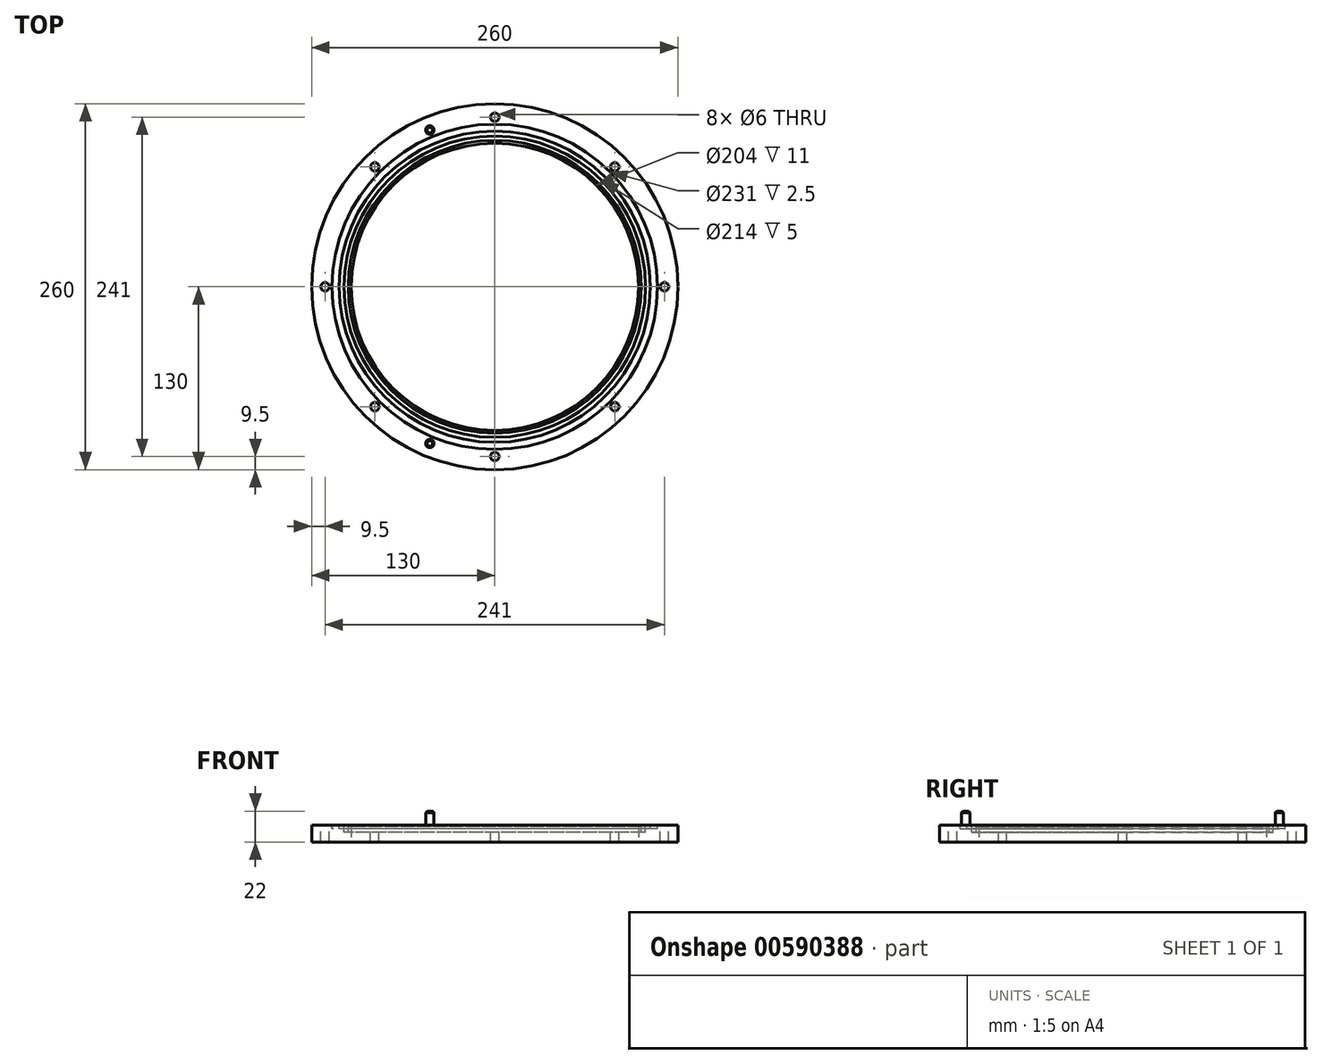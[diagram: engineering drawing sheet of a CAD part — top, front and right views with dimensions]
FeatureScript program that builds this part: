
annotation { "Feature Type Name" : "Feature", "Feature Type Description" : "" }
export const myFeature = defineFeature(function(context is Context, id is Id, definition is map)
    precondition{}
    {
        {
            var Q0;
            Q0=qCreatedBy(makeId("Top.planeOp"),FACE);
            var sketch = newSketch(context, id + "F0", { "sketchPlane" : qUnion([Q0])});
            skCircle(sketch, "E0", {"center": v(0, 0) * mm, "radius": 130 * mm});
            skCircle(sketch, "E1", {"center": v(0, 0) * mm, "radius": 102 * mm});
            skSolve(sketch);
        }
        {
            var Q0;
            Q0=makeQuery(id+"F0.imprint","IMPRINT",FACE,{"disambiguationData":[TD([[makeQuery(id+"F0.imprint","IMPRINT",EDGE,{"derivedFrom":sQuery(id+"F0.wireOp",EDGE,"E0")}),1.0]])]});
            extrude(context, id + "F1", {"entities" : qUnion([Q0]), "depth" : 12 * mm, "offsetDistance" : 25 * mm});
        }
        {
            var Q0;
            Q0=makeQuery(id+"F1.opExtrude","CAP_FACE",FACE,{"disambiguationData":[OSD([sQuery(id+"F0.wireOp",EDGE,"E0"),sQuery(id+"F0.wireOp",EDGE,"E1")])],"isStart":false});
            var sketch = newSketch(context, id + "F2", { "sketchPlane" : qUnion([Q0])});
            skCircle(sketch, "E2", {"center": v(0, 0) * mm, "radius": 115.5 * mm});
            skCircle(sketch, "E3", {"center": v(0, 0) * mm, "radius": 110.5 * mm});
            skSolve(sketch);
        }
        {
            var Q0;
            Q0=makeQuery(id+"F2.imprint","IMPRINT",FACE,{"disambiguationData":[TD([[makeQuery(id+"F2.imprint","IMPRINT",EDGE,{"derivedFrom":sQuery(id+"F2.wireOp",EDGE,"E2")}),1.0]])]});
            extrude(context, id + "F3", {"entities" : qUnion([Q0]), "operationType" : NewBodyOperationType.REMOVE, "oppositeDirection" : true, "depth" : 2.5 * mm, "offsetDistance" : 25 * mm});
        }
        {
            var Q0;
            {var subQ0=sQuery(id+"F0.wireOp",EDGE,"E1");Q0=makeQuery(id+"F3.boolean.opBoolean","SPLIT",FACE,{"disambiguationData":[TD([makeQuery(id+"F1.opExtrude","SWEPT_FACE",FACE,{"disambiguationData":[OSD([subQ0])]})])],"derivedFrom":makeQuery(id+"F1.opExtrude","CAP_FACE",FACE,{"disambiguationData":[OSD([sQuery(id+"F0.wireOp",EDGE,"E0"),subQ0])],"isStart":false})});}
            var sketch = newSketch(context, id + "F4", { "sketchPlane" : qUnion([Q0])});
            skCircle(sketch, "E4", {"center": v(0, 0) * mm, "radius": 107 * mm});
            skCircle(sketch, "E5", {"center": v(0, 0) * mm, "radius": 104 * mm});
            skSolve(sketch);
        }
        {
            var Q0;
            Q0=makeQuery(id+"F4.imprint","IMPRINT",FACE,{"disambiguationData":[TD([[makeQuery(id+"F4.imprint","IMPRINT",EDGE,{"derivedFrom":sQuery(id+"F4.wireOp",EDGE,"E4")}),1.0]])]});
            extrude(context, id + "F5", {"entities" : qUnion([Q0]), "operationType" : NewBodyOperationType.REMOVE, "oppositeDirection" : true, "depth" : 5 * mm, "offsetDistance" : 25 * mm});
        }
        {
            var Q0;
            {var subQ0=sQuery(id+"F0.wireOp",EDGE,"E1");var subQ1=makeQuery(id+"F1.opExtrude","SWEPT_FACE",FACE,{"disambiguationData":[OSD([subQ0])]});Q0=makeQuery(id+"F5.boolean.opBoolean","SPLIT",FACE,{"disambiguationData":[TD([subQ1])],"derivedFrom":makeQuery(id+"F3.boolean.opBoolean","SPLIT",FACE,{"disambiguationData":[TD([subQ1])],"derivedFrom":makeQuery(id+"F1.opExtrude","CAP_FACE",FACE,{"disambiguationData":[OSD([sQuery(id+"F0.wireOp",EDGE,"E0"),subQ0])],"isStart":false})})});}
            var sketch = newSketch(context, id + "F6", { "sketchPlane" : qUnion([Q0])});
            skCircle(sketch, "E6", {"center": v(0, 0) * mm, "radius": 104 * mm});
            skCircle(sketch, "E7", {"center": v(0, 0) * mm, "radius": 102 * mm});
            skSolve(sketch);
        }
        {
            var Q0;
            Q0=makeQuery(id+"F6.imprint","IMPRINT",FACE,{"disambiguationData":[TD([[makeQuery(id+"F6.imprint","IMPRINT",EDGE,{"derivedFrom":sQuery(id+"F6.wireOp",EDGE,"E6")}),1.0]])]});
            extrude(context, id + "F7", {"entities" : qUnion([Q0]), "operationType" : NewBodyOperationType.REMOVE, "oppositeDirection" : true, "depth" : 1 * mm, "offsetDistance" : 25 * mm});
        }
        {
            var Q0;
            {var subQ0=sQuery(id+"F0.wireOp",EDGE,"E0");Q0=makeQuery(id+"F3.boolean.opBoolean","SPLIT",FACE,{"disambiguationData":[TD([makeQuery(id+"F1.opExtrude","SWEPT_FACE",FACE,{"disambiguationData":[OSD([subQ0])]})])],"derivedFrom":makeQuery(id+"F1.opExtrude","CAP_FACE",FACE,{"disambiguationData":[OSD([subQ0,sQuery(id+"F0.wireOp",EDGE,"E1")])],"isStart":false})});}
            var sketch = newSketch(context, id + "F8", { "sketchPlane" : qUnion([Q0])});
            skLineSegment(sketch, "E8", {"start": v(0, 0) * mm, "end": v(0, 130) * mm, "construction": true});
            skLineSegment(sketch, "E9", {"start": v(0, 0) * mm, "end": v(130, 0) * mm, "construction": true});
            skLineSegment(sketch, "E10", {"start": v(0, 0) * mm, "end": v(-130, 0) * mm, "construction": true});
            skLineSegment(sketch, "E11", {"start": v(0, 0) * mm, "end": v(0, -130) * mm, "construction": true});
            skLineSegment(sketch, "E12", {"start": v(0, 0) * mm, "end": v(-91.92, 91.92) * mm, "construction": true});
            skLineSegment(sketch, "E13", {"start": v(0, 0) * mm, "end": v(91.92, 91.92) * mm, "construction": true});
            skLineSegment(sketch, "E14", {"start": v(0, 0) * mm, "end": v(91.92, -91.92) * mm, "construction": true});
            skLineSegment(sketch, "E15", {"start": v(0, 0) * mm, "end": v(-91.92, -91.92) * mm, "construction": true});
            skLineSegment(sketch, "E16", {"start": v(0, 0) * mm, "end": v(-49.75, 120.1) * mm, "construction": true});
            skCircle(sketch, "E17", {"center": v(-120.5, 0) * mm, "radius": 3 * mm});
            skCircle(sketch, "E18", {"center": v(-85.2, 85.2) * mm, "radius": 3 * mm});
            skCircle(sketch, "E19", {"center": v(0, 120.5) * mm, "radius": 3 * mm});
            skCircle(sketch, "E20", {"center": v(0, -120.5) * mm, "radius": 3 * mm});
            skCircle(sketch, "E21", {"center": v(-85.2, -85.2) * mm, "radius": 3 * mm});
            skCircle(sketch, "E22", {"center": v(85.2, -85.2) * mm, "radius": 3 * mm});
            skCircle(sketch, "E23", {"center": v(120.5, 0) * mm, "radius": 3 * mm});
            skCircle(sketch, "E24", {"center": v(85.2, 85.2) * mm, "radius": 3 * mm});
            skLineSegment(sketch, "E25", {"start": v(0, 0) * mm, "end": v(-49.75, -120.1) * mm, "construction": true});
            skCircle(sketch, "E26", {"center": v(-46.11, -111.33) * mm, "radius": 3 * mm});
            skCircle(sketch, "E27", {"center": v(-46.11, 111.33) * mm, "radius": 3 * mm});
            skSolve(sketch);
        }
        {
            var Q0;
            Q0=makeQuery(id+"F8.imprint","IMPRINT",FACE,{"disambiguationData":[TD([[makeQuery(id+"F8.imprint","IMPRINT",EDGE,{"derivedFrom":sQuery(id+"F8.wireOp",EDGE,"E17")}),1.0]])]});
            var Q1;
            Q1=makeQuery(id+"F8.imprint","IMPRINT",FACE,{"disambiguationData":[TD([[makeQuery(id+"F8.imprint","IMPRINT",EDGE,{"derivedFrom":sQuery(id+"F8.wireOp",EDGE,"E18")}),1.0]])]});
            var Q2;
            Q2=makeQuery(id+"F8.imprint","IMPRINT",FACE,{"disambiguationData":[TD([[makeQuery(id+"F8.imprint","IMPRINT",EDGE,{"derivedFrom":sQuery(id+"F8.wireOp",EDGE,"E19")}),1.0]])]});
            var Q3;
            Q3=makeQuery(id+"F8.imprint","IMPRINT",FACE,{"disambiguationData":[TD([[makeQuery(id+"F8.imprint","IMPRINT",EDGE,{"derivedFrom":sQuery(id+"F8.wireOp",EDGE,"E23")}),1.0]])]});
            var Q4;
            Q4=makeQuery(id+"F8.imprint","IMPRINT",FACE,{"disambiguationData":[TD([[makeQuery(id+"F8.imprint","IMPRINT",EDGE,{"derivedFrom":sQuery(id+"F8.wireOp",EDGE,"E24")}),1.0]])]});
            var Q5;
            Q5=makeQuery(id+"F8.imprint","IMPRINT",FACE,{"disambiguationData":[TD([[makeQuery(id+"F8.imprint","IMPRINT",EDGE,{"derivedFrom":sQuery(id+"F8.wireOp",EDGE,"E22")}),1.0]])]});
            var Q6;
            Q6=makeQuery(id+"F8.imprint","IMPRINT",FACE,{"disambiguationData":[TD([[makeQuery(id+"F8.imprint","IMPRINT",EDGE,{"derivedFrom":sQuery(id+"F8.wireOp",EDGE,"E20")}),1.0]])]});
            var Q7;
            Q7=makeQuery(id+"F8.imprint","IMPRINT",FACE,{"disambiguationData":[TD([[makeQuery(id+"F8.imprint","IMPRINT",EDGE,{"derivedFrom":sQuery(id+"F8.wireOp",EDGE,"E21")}),1.0]])]});
            extrude(context, id + "F9", {"entities" : qUnion([Q0, Q1, Q2, Q3, Q4, Q5, Q6, Q7]), "operationType" : NewBodyOperationType.REMOVE, "oppositeDirection" : true, "depth" : 12 * mm, "offsetDistance" : 25 * mm});
        }
        {
            var Q0;
            Q0=makeQuery(id+"F8.imprint","IMPRINT",FACE,{"disambiguationData":[TD([[makeQuery(id+"F8.imprint","IMPRINT",EDGE,{"derivedFrom":sQuery(id+"F8.wireOp",EDGE,"E27")}),1.0]])]});
            var Q1;
            Q1=makeQuery(id+"F8.imprint","IMPRINT",FACE,{"disambiguationData":[TD([[makeQuery(id+"F8.imprint","IMPRINT",EDGE,{"derivedFrom":sQuery(id+"F8.wireOp",EDGE,"E26")}),1.0]])]});
            extrude(context, id + "F10", {"entities" : qUnion([Q0, Q1]), "operationType" : NewBodyOperationType.ADD, "depth" : 10 * mm, "offsetDistance" : 25 * mm});
        }
        {
            var Q0;
            Q0=makeQuery(id+"F10.opExtrude","CAP_EDGE",EDGE,{"disambiguationData":[OSD([sQuery(id+"F8.wireOp",EDGE,"E26")])],"isStart":false});
            chamfer(context, id + "F11", {"entities" : qUnion([Q0]), "width" : 1 * mm, "tangentPropagation" : true});
        }
        {
            var Q0;
            Q0=makeQuery(id+"F10.opExtrude","CAP_EDGE",EDGE,{"disambiguationData":[OSD([sQuery(id+"F8.wireOp",EDGE,"E27")])],"isStart":false});
            chamfer(context, id + "F12", {"entities" : qUnion([Q0]), "width" : 1 * mm, "tangentPropagation" : true});
        }
    });
